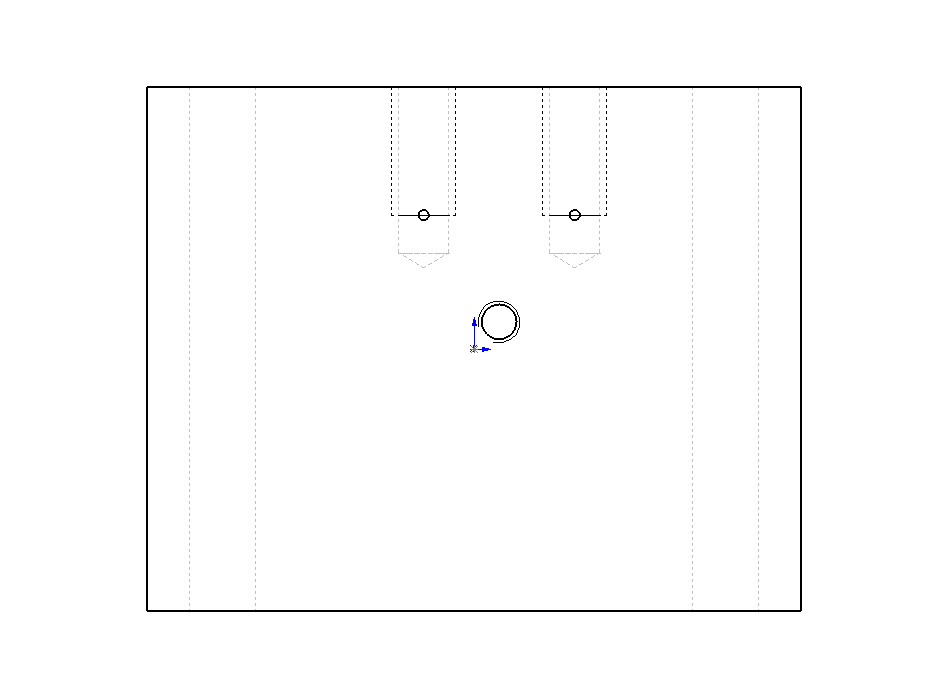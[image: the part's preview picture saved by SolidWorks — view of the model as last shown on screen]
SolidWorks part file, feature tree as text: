
SOLIDWORKS PART (.sldprt)
format: sldprt  version: not decoded by parser v0  size: 477,696 bytes
history: native  units: mm
features: sketch x8, hole x3, thread x3, material x1, extrude x1, cut_extrude x1 (+12 scaffold rows collapsed)
feature tree (29):
  scaffold x12  (default folders/planes/origin — collapsed)
  material  "Material <not specified>"
  sketch  "Sketch1"  dims[c1.D1=0.0mm c1.D2=65.0mm c2.D1=52.0mm]
  extrude  "Base-Extrude"  Depth=15mm
  hole  "1/4-20 Tapped Hole1"  Diameter=5.1054mm Depth=16.51mm
  sketch  "Sketch3"  dims[c1.D1=22.5mm c1.D2=40.0mm c2.D1=22.5mm c2.D2=37.5mm]
  sketch  "Sketch2"  dims[hole-wizard template sketch: 50 standard entries collapsed; hole parameters above]
  thread  "Cosmetic Thread1"  Diameter=12.7mm  [1 undecoded]
  thread  "Cosmetic Thread2"  Diameter=12.7mm  [1 undecoded]
  hole  "1/4 Clearance Hole1"  Diameter=6.7564mm Depth=52mm
  sketch  "Sketch5"  dims[D1=7.5mm D2=57.5mm]
  sketch  "Sketch4"  dims[hole-wizard template sketch: 60 standard entries collapsed; hole parameters kept: c18.Thru Hole Depth=52.0mm]
  hole  "#8-32 Tapped Hole1"  Diameter=3.4544mm Depth=15mm
  sketch  "Sketch7"  dims[D1=35.0mm D2=28.7mm]
  sketch  "Sketch6"  dims[hole-wizard template sketch: 60 standard entries collapsed; hole parameters kept: c18.Thru Tap Drill Depth=15.0mm]
  thread  "Cosmetic Thread3"  Diameter=4.1656mm  [1 undecoded]
  sketch  "Sketch8"  dims[c1.D2=1.016mm c1.D3=1.016mm c1.D1=12.7mm c2.D3=~14.98627mm]
  cut_extrude  "Cut-Extrude1"  [1 undecoded]
decode coverage: 15 of 16 modeling features carry decoded parameters
note: ~ marks probable driven/reference dimensions
note: 4 parameter values undecoded
note: suppression state not decoded; provenance and decode notes live in map.json
